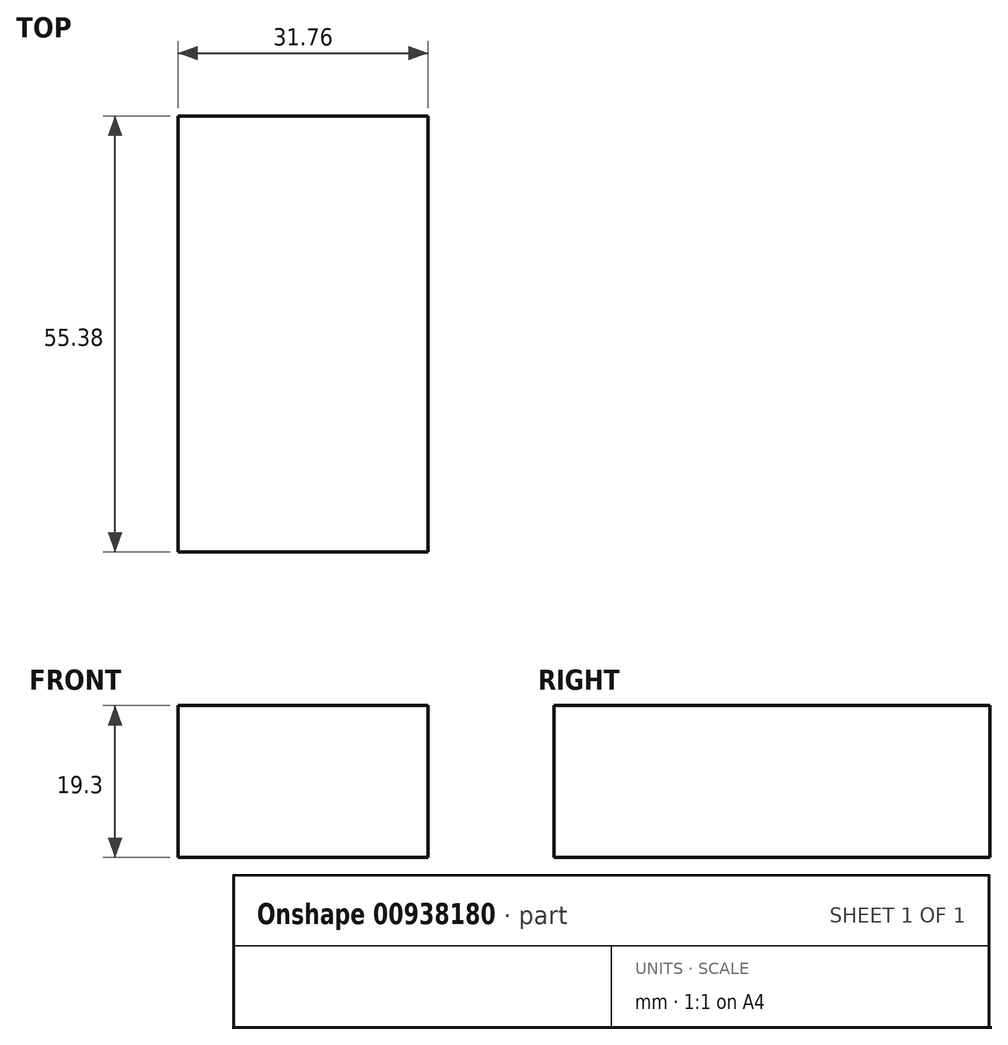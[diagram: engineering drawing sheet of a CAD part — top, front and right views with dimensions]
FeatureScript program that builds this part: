
annotation { "Feature Type Name" : "Feature", "Feature Type Description" : "" }
export const myFeature = defineFeature(function(context is Context, id is Id, definition is map)
    precondition{}
    {
        {
            var Q0;
            Q0=qCreatedBy(makeId("Top.planeOp"),FACE);
            var sketch = newSketch(context, id + "F0", { "sketchPlane" : qUnion([Q0])});
            skLineSegment(sketch, "E0.bottom", {"start": v(15.88, 27.69) * mm, "end": v(-15.87, 27.69) * mm});
            skLineSegment(sketch, "E0.top", {"start": v(15.87, -27.69) * mm, "end": v(-15.88, -27.69) * mm});
            skLineSegment(sketch, "E0.left", {"start": v(15.88, 27.69) * mm, "end": v(15.87, -27.69) * mm});
            skLineSegment(sketch, "E0.right", {"start": v(-15.87, 27.69) * mm, "end": v(-15.88, -27.69) * mm});
            skPoint(sketch, "E0.middle", {"position": v(0, 0) * mm});
            skSolve(sketch);
        }
        {
            var Q0;
            Q0=makeQuery(id+"F0.imprint","IMPRINT",FACE,{"disambiguationData":[TD([[makeQuery(id+"F0.imprint","IMPRINT",EDGE,{"derivedFrom":sQuery(id+"F0.wireOp",EDGE,"E0.bottom")}),1.0]])]});
            extrude(context, id + "F1", {"entities" : qUnion([Q0]), "depth" : 19.3 * mm, "offsetDistance" : 25.4 * mm});
        }
    });
